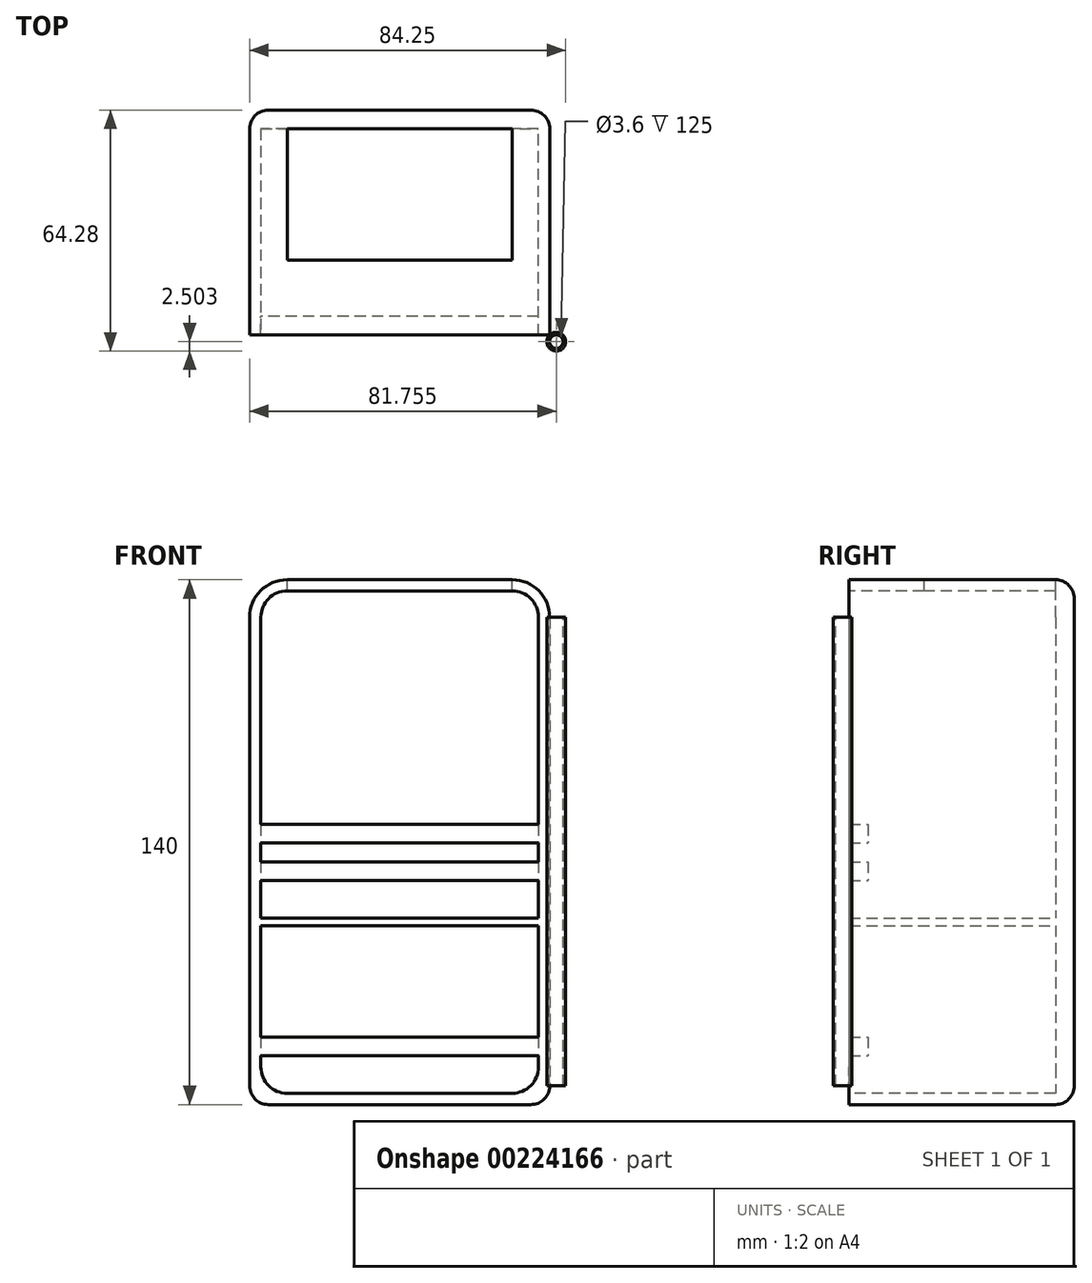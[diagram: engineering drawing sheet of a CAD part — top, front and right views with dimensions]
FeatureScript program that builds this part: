
annotation { "Feature Type Name" : "Feature", "Feature Type Description" : "" }
export const myFeature = defineFeature(function(context is Context, id is Id, definition is map)
    precondition{}
    {
        {
            var Q0;
            Q0=qCreatedBy(makeId("Top.planeOp"),FACE);
            var sketch = newSketch(context, id + "F0", { "sketchPlane" : qUnion([Q0])});
            skLineSegment(sketch, "E0.bottom", {"start": v(-45.23, 15.92) * mm, "end": v(34.77, 15.92) * mm});
            skLineSegment(sketch, "E0.top", {"start": v(-45.23, -44.08) * mm, "end": v(34.77, -44.08) * mm});
            skLineSegment(sketch, "E0.left", {"start": v(-45.23, 15.92) * mm, "end": v(-45.23, -44.08) * mm});
            skLineSegment(sketch, "E0.right", {"start": v(34.77, 15.92) * mm, "end": v(34.77, -44.08) * mm});
            skSolve(sketch);
        }
        {
            var Q0;
            Q0=makeQuery(id+"F0.imprint","IMPRINT",FACE,{"disambiguationData":[TD([[makeQuery(id+"F0.imprint","IMPRINT",EDGE,{"derivedFrom":sQuery(id+"F0.wireOp",EDGE,"E0.bottom")}),-1.0]])]});
            extrude(context, id + "F1", {"entities" : qUnion([Q0]), "depth" : 140 * mm});
        }
        {
            var Q0;
            Q0=makeQuery(id+"F1.opExtrude","CAP_EDGE",EDGE,{"disambiguationData":[OSD([sQuery(id+"F0.wireOp",EDGE,"E0.left")])],"isStart":false});
            fillet(context, id + "F2", {"entities" : qUnion([Q0]), "radius" : 10 * mm, "tangentPropagation" : true, "allowEdgeOverflow" : false});
        }
        {
            var Q0;
            Q0=makeQuery(id+"F1.opExtrude","CAP_EDGE",EDGE,{"disambiguationData":[OSD([sQuery(id+"F0.wireOp",EDGE,"E0.right")])],"isStart":false});
            fillet(context, id + "F3", {"entities" : qUnion([Q0]), "radius" : 10 * mm, "tangentPropagation" : true, "allowEdgeOverflow" : false});
        }
        {
            var Q0;
            Q0=makeQuery(id+"F1.opExtrude","CAP_EDGE",EDGE,{"disambiguationData":[OSD([sQuery(id+"F0.wireOp",EDGE,"E0.left")])],"isStart":true});
            fillet(context, id + "F4", {"entities" : qUnion([Q0]), "radius" : 5 * mm, "tangentPropagation" : true, "allowEdgeOverflow" : false});
        }
        {
            var Q0;
            Q0=makeQuery(id+"F1.opExtrude","CAP_EDGE",EDGE,{"disambiguationData":[OSD([sQuery(id+"F0.wireOp",EDGE,"E0.right")])],"isStart":true});
            fillet(context, id + "F5", {"entities" : qUnion([Q0]), "radius" : 5 * mm, "tangentPropagation" : true, "allowEdgeOverflow" : false});
        }
        {
            var Q0;
            Q0=makeQuery(id+"F1.opExtrude","SWEPT_FACE",FACE,{"disambiguationData":[OSD([sQuery(id+"F0.wireOp",EDGE,"E0.top")])]});
            var sketch = newSketch(context, id + "F6", { "sketchPlane" : qUnion([Q0])});
            skLineSegment(sketch, "E1.bottom", {"start": v(-35.23, 137) * mm, "end": v(24.77, 137) * mm});
            skLineSegment(sketch, "E1.top", {"start": v(-35.23, 3) * mm, "end": v(24.77, 3) * mm});
            skLineSegment(sketch, "E1.left", {"start": v(-42.23, 130) * mm, "end": v(-42.23, 10) * mm});
            skLineSegment(sketch, "E1.right", {"start": v(31.77, 130) * mm, "end": v(31.77, 10) * mm});
            skPoint(sketch, "E2.visualSharp", {"position": v(-42.23, 137) * mm});
            skArc(sketch, "E2.filletArc", {"start": v(-35.23, 137) * mm, "mid": v(-40.18, 134.95) * mm, "end": v(-42.23, 130) * mm});
            skPoint(sketch, "E3.visualSharp", {"position": v(31.77, 137) * mm});
            skArc(sketch, "E3.filletArc", {"start": v(31.77, 130) * mm, "mid": v(29.72, 134.95) * mm, "end": v(24.77, 137) * mm});
            skPoint(sketch, "E4.visualSharp", {"position": v(31.77, 3) * mm});
            skArc(sketch, "E4.filletArc", {"start": v(24.77, 3) * mm, "mid": v(29.72, 5.05) * mm, "end": v(31.77, 10) * mm});
            skPoint(sketch, "E5.visualSharp", {"position": v(-42.23, 3) * mm});
            skArc(sketch, "E5.filletArc", {"start": v(-42.23, 10) * mm, "mid": v(-40.18, 5.05) * mm, "end": v(-35.23, 3) * mm});
            skSolve(sketch);
        }
        {
            var Q0;
            Q0=makeQuery(id+"F6.imprint","IMPRINT",FACE,{"disambiguationData":[TD([[makeQuery(id+"F6.imprint","IMPRINT",EDGE,{"derivedFrom":sQuery(id+"F6.wireOp",EDGE,"E1.bottom")}),-1.0]])]});
            extrude(context, id + "F7", {"entities" : qUnion([Q0]), "operationType" : NewBodyOperationType.REMOVE, "oppositeDirection" : true, "depth" : 55 * mm});
        }
        {
            var Q0;
            Q0=makeQuery(id+"F7.boolean.opBoolean","COPY",FACE,{"derivedFrom":makeQuery(id+"F7.opExtrude","CAP_FACE",FACE,{"disambiguationData":[OSD([sQuery(id+"F6.wireOp",EDGE,"E1.bottom"),sQuery(id+"F6.wireOp",EDGE,"E1.top"),sQuery(id+"F6.wireOp",EDGE,"E1.left"),sQuery(id+"F6.wireOp",EDGE,"E1.right"),sQuery(id+"F6.wireOp",EDGE,"E2.filletArc"),sQuery(id+"F6.wireOp",EDGE,"E3.filletArc"),sQuery(id+"F6.wireOp",EDGE,"E4.filletArc"),sQuery(id+"F6.wireOp",EDGE,"E5.filletArc")])],"isStart":false})});
            var sketch = newSketch(context, id + "F8", { "sketchPlane" : qUnion([Q0])});
            skLineSegment(sketch, "E6", {"start": v(-42.23, 48) * mm, "end": v(31.77, 48) * mm});
            skSolve(sketch);
        }
        {
            var Q0;
            {var subQ2=sQuery(id+"F8.wireOp",EDGE,"E6");Q0=makeQuery(id+"F8.imprint","IMPRINT",FACE,{"disambiguationData":[TD([[makeQuery(id+"F8.imprint","IMPRINT",EDGE,{"derivedFrom":subQ2}),1.0]])]});}
            var sketch = newSketch(context, id + "F9", { "sketchPlane" : qUnion([Q0])});
            skLineSegment(sketch, "E7.bottom", {"start": v(-42.23, 47.75) * mm, "end": v(31.77, 47.75) * mm});
            skLineSegment(sketch, "E7.top", {"start": v(-42.23, 49.75) * mm, "end": v(31.77, 49.75) * mm});
            skLineSegment(sketch, "E7.left", {"start": v(-42.23, 47.75) * mm, "end": v(-42.23, 49.75) * mm});
            skLineSegment(sketch, "E7.right", {"start": v(31.77, 47.75) * mm, "end": v(31.77, 49.75) * mm});
            skSolve(sketch);
        }
        {
            var Q0;
            Q0 = qSketchRegion(id + "F9", true);
            extrude(context, id + "F10", {"entities" : qUnion([Q0]), "operationType" : NewBodyOperationType.ADD, "depth" : 55 * mm});
        }
        {
            var Q0;
            Q0=makeQuery(id+"F1.opExtrude","CAP_FACE",FACE,{"disambiguationData":[OSD([sQuery(id+"F0.wireOp",EDGE,"E0.bottom"),sQuery(id+"F0.wireOp",EDGE,"E0.top"),sQuery(id+"F0.wireOp",EDGE,"E0.left"),sQuery(id+"F0.wireOp",EDGE,"E0.right")])],"isStart":false});
            var sketch = newSketch(context, id + "F11", { "sketchPlane" : qUnion([Q0])});
            skLineSegment(sketch, "E8.bottom", {"start": v(-35.23, 10.92) * mm, "end": v(24.77, 10.92) * mm});
            skLineSegment(sketch, "E8.top", {"start": v(-35.23, -24.08) * mm, "end": v(24.77, -24.08) * mm});
            skLineSegment(sketch, "E8.left", {"start": v(-35.23, 10.92) * mm, "end": v(-35.23, -24.08) * mm});
            skLineSegment(sketch, "E8.right", {"start": v(24.77, 10.92) * mm, "end": v(24.77, -24.08) * mm});
            skSolve(sketch);
        }
        {
            var Q0;
            Q0=makeQuery(id+"F11.imprint","IMPRINT",FACE,{"disambiguationData":[TD([[makeQuery(id+"F11.imprint","IMPRINT",EDGE,{"derivedFrom":sQuery(id+"F11.wireOp",EDGE,"E8.bottom")}),-1.0]])]});
            extrude(context, id + "F12", {"entities" : qUnion([Q0]), "operationType" : NewBodyOperationType.REMOVE, "oppositeDirection" : true, "depth" : 28 * mm});
        }
        {
            var Q0;
            Q0=makeQuery(id+"F1.opExtrude","CAP_EDGE",EDGE,{"disambiguationData":[OSD([sQuery(id+"F0.wireOp",EDGE,"E0.bottom")])],"isStart":false});
            fillet(context, id + "F13", {"entities" : qUnion([Q0]), "radius" : 5 * mm, "tangentPropagation" : true, "allowEdgeOverflow" : false});
        }
        {
            var Q0;
            {var subQ1=sQuery(id+"F6.wireOp",EDGE,"E2.filletArc");var subQ2=sQuery(id+"F6.wireOp",EDGE,"E1.left");Q0=makeQuery(id+"F10.boolean.opBoolean","SPLIT",FACE,{"disambiguationData":[TD([makeQuery(id+"F7.boolean.opBoolean","COPY",FACE,{"derivedFrom":makeQuery(id+"F7.opExtrude","SWEPT_FACE",FACE,{"disambiguationData":[OSD([subQ1])]})})])],"derivedFrom":makeQuery(id+"F7.boolean.opBoolean","COPY",FACE,{"derivedFrom":makeQuery(id+"F7.opExtrude","SWEPT_FACE",FACE,{"disambiguationData":[OSD([subQ2])]})})});}
            var sketch = newSketch(context, id + "F14", { "sketchPlane" : qUnion([Q0])});
            skLineSegment(sketch, "E9.bottom", {"start": v(-44.08, 64.75) * mm, "end": v(-39.08, 64.75) * mm});
            skLineSegment(sketch, "E9.top", {"start": v(-44.08, 59.75) * mm, "end": v(-39.08, 59.75) * mm});
            skLineSegment(sketch, "E9.left", {"start": v(-44.08, 64.75) * mm, "end": v(-44.08, 59.75) * mm});
            skLineSegment(sketch, "E9.right", {"start": v(-39.08, 64.75) * mm, "end": v(-39.08, 59.75) * mm});
            skSolve(sketch);
        }
        {
            var Q0;
            Q0 = qSketchRegion(id + "F14", true);
            extrude(context, id + "F15", {"entities" : qUnion([Q0]), "operationType" : NewBodyOperationType.ADD, "depth" : 74 * mm});
        }
        {
            var Q0;
            {var subQ1=sQuery(id+"F6.wireOp",EDGE,"E2.filletArc");var subQ2=sQuery(id+"F6.wireOp",EDGE,"E1.left");Q0=makeQuery(id+"F10.boolean.opBoolean","SPLIT",FACE,{"disambiguationData":[TD([makeQuery(id+"F7.boolean.opBoolean","COPY",FACE,{"derivedFrom":makeQuery(id+"F7.opExtrude","SWEPT_FACE",FACE,{"disambiguationData":[OSD([subQ1])]})})])],"derivedFrom":makeQuery(id+"F7.boolean.opBoolean","COPY",FACE,{"derivedFrom":makeQuery(id+"F7.opExtrude","SWEPT_FACE",FACE,{"disambiguationData":[OSD([subQ2])]})})});}
            var sketch = newSketch(context, id + "F16", { "sketchPlane" : qUnion([Q0])});
            skLineSegment(sketch, "E10.bottom", {"start": v(-44.08, 74.75) * mm, "end": v(-39.08, 74.75) * mm});
            skLineSegment(sketch, "E10.top", {"start": v(-44.08, 69.75) * mm, "end": v(-39.08, 69.75) * mm});
            skLineSegment(sketch, "E10.left", {"start": v(-44.08, 74.75) * mm, "end": v(-44.08, 69.75) * mm});
            skLineSegment(sketch, "E10.right", {"start": v(-39.08, 74.75) * mm, "end": v(-39.08, 69.75) * mm});
            skSolve(sketch);
        }
        {
            var Q0;
            Q0 = qSketchRegion(id + "F16", true);
            var Q1;
            Q1 = qSketchRegion(id + "F18", true);
            extrude(context, id + "F17", {"entities" : qUnion([Q0, Q1]), "operationType" : NewBodyOperationType.ADD, "depth" : 74 * mm});
        }
        {
            var Q0;
            Q0=qCreatedBy(makeId("Top.planeOp"),FACE);
            var sketch = newSketch(context, id + "F18", { "sketchPlane" : qUnion([Q0])});
            skCircle(sketch, "E11", {"center": v(36.52, -45.86) * mm, "radius": 2.5 * mm});
            skSolve(sketch);
        }
        {
            var Q0;
            Q0=makeQuery(id+"F18.imprint","IMPRINT",FACE,{"disambiguationData":[TD([[makeQuery(id+"F18.imprint","IMPRINT",EDGE,{"derivedFrom":sQuery(id+"F18.wireOp",EDGE,"E11")}),1.0]])]});
            extrude(context, id + "F19", {"entities" : qUnion([Q0]), "operationType" : NewBodyOperationType.ADD, "depth" : 130 * mm});
        }
        {
            var Q0;
            Q0=makeQuery(id+"F19.opExtrude","CAP_FACE",FACE,{"disambiguationData":[OSD([sQuery(id+"F18.wireOp",EDGE,"E11")])],"isStart":true});
            extrude(context, id + "F20", {"entities" : qUnion([Q0]), "operationType" : NewBodyOperationType.REMOVE, "oppositeDirection" : true, "depth" : 5 * mm});
        }
        {
            var Q0;
            {var subQ1=sQuery(id+"F6.wireOp",EDGE,"E5.filletArc");var subQ2=sQuery(id+"F6.wireOp",EDGE,"E1.left");Q0=makeQuery(id+"F10.boolean.opBoolean","SPLIT",FACE,{"disambiguationData":[TD([makeQuery(id+"F7.boolean.opBoolean","COPY",FACE,{"derivedFrom":makeQuery(id+"F7.opExtrude","SWEPT_FACE",FACE,{"disambiguationData":[OSD([subQ1])]})})])],"derivedFrom":makeQuery(id+"F7.boolean.opBoolean","COPY",FACE,{"derivedFrom":makeQuery(id+"F7.opExtrude","SWEPT_FACE",FACE,{"disambiguationData":[OSD([subQ2])]})})});}
            var sketch = newSketch(context, id + "F21", { "sketchPlane" : qUnion([Q0])});
            skLineSegment(sketch, "E12.bottom", {"start": v(-44.08, 18) * mm, "end": v(-39.08, 18) * mm});
            skLineSegment(sketch, "E12.top", {"start": v(-44.08, 13) * mm, "end": v(-39.08, 13) * mm});
            skLineSegment(sketch, "E12.left", {"start": v(-44.08, 18) * mm, "end": v(-44.08, 13) * mm});
            skLineSegment(sketch, "E12.right", {"start": v(-39.08, 18) * mm, "end": v(-39.08, 13) * mm});
            skSolve(sketch);
        }
        {
            var Q0;
            Q0 = qSketchRegion(id + "F21", true);
            extrude(context, id + "F22", {"entities" : qUnion([Q0]), "operationType" : NewBodyOperationType.ADD, "depth" : 74 * mm});
        }
        {
            var Q0;
            Q0=makeQuery(id+"F19.opExtrude","CAP_FACE",FACE,{"disambiguationData":[OSD([sQuery(id+"F18.wireOp",EDGE,"E11")])],"isStart":false});
            var sketch = newSketch(context, id + "F23", { "sketchPlane" : qUnion([Q0])});
            skCircle(sketch, "E13", {"center": v(36.52, -45.86) * mm, "radius": 1.8 * mm});
            skSolve(sketch);
        }
        {
            var Q0;
            Q0 = qSketchRegion(id + "F23", true);
            extrude(context, id + "F24", {"entities" : qUnion([Q0]), "operationType" : NewBodyOperationType.REMOVE, "oppositeDirection" : true, "depth" : 132 * mm});
        }
    });
